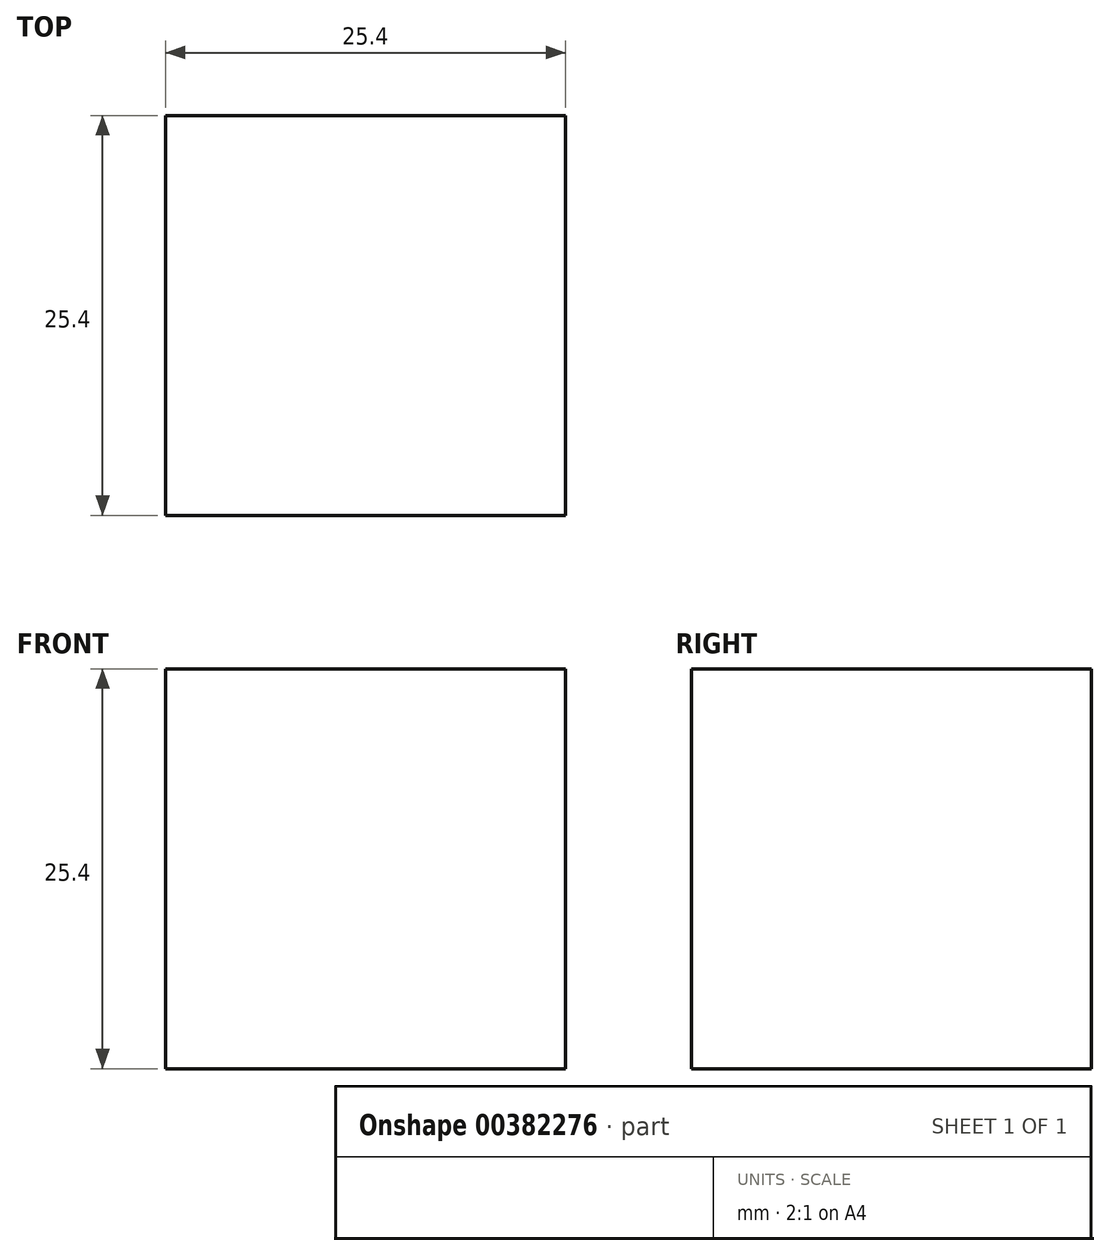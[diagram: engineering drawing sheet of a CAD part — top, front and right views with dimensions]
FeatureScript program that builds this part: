
annotation { "Feature Type Name" : "Feature", "Feature Type Description" : "" }
export const myFeature = defineFeature(function(context is Context, id is Id, definition is map)
    precondition{}
    {
        {
            var Q0;
            Q0=qCreatedBy(makeId("Front.planeOp"),FACE);
            var sketch = newSketch(context, id + "F0", { "sketchPlane" : qUnion([Q0])});
            skLineSegment(sketch, "E0.bottom", {"start": v(0, 0) * mm, "end": v(25.4, 0) * mm});
            skLineSegment(sketch, "E0.top", {"start": v(0, 25.4) * mm, "end": v(25.4, 25.4) * mm});
            skLineSegment(sketch, "E0.left", {"start": v(0, 0) * mm, "end": v(0, 25.4) * mm});
            skLineSegment(sketch, "E0.right", {"start": v(25.4, 0) * mm, "end": v(25.4, 25.4) * mm});
            skSolve(sketch);
        }
        {
            var Q0;
            Q0=makeQuery(id+"F0.imprint","IMPRINT",FACE,{"disambiguationData":[TD([[makeQuery(id+"F0.imprint","IMPRINT",EDGE,{"derivedFrom":sQuery(id+"F0.wireOp",EDGE,"E0.bottom")}),1.0]])]});
            extrude(context, id + "F1", {"entities" : qUnion([Q0]), "endBound" : BoundingType.SYMMETRIC, "depth" : 25.4 * mm});
        }
    });
